# Revit family: Seating_Inc-Hip_Chairs-Cobra-1
name_source: partatom
category: Furniture
revit_build: Autodesk Revit 2014 (Build: 20130308_1515(x64)
units: mm (PartAtom-declared; Revit-internal decimal feet)

## types (4) — shared parameters
Arm Left = Yes
Arm Plastic Finish = STI - Plastic Black
Arm Right = Yes
Assembly Code = E2020200
Back Finish = STI - Upholstery Latex
Depth = 25 1/2"
Glide Finish = STI - Plastic Black
Height = 25"
Keynote = 12500
Low Emitting Finish = Yes
Low Emitting Material = Yes
Manufacturer = Seating Inc
Salvage or Reuse = Yes
Seat Finish = STI - Upholstery Latex
Type Comments = Cobra Tandem Seating
URL = www.seatinginc.com
zero-valued in all types: Percentage of Recycled Content

## per-type parameters (varying)
| type | Arm | Arm Metal Finish | Description | Leg Finish | Support Finish | Width |
| CS444-21B | 23" | STI - Power Coat, Black | Black w/Arms | STI - Power Coat, Black | STI - Power Coat, Black | 23" |
| CS444-21S | 23" | STI - Power Coat, Silver | Silver w/Arms | STI - Power Coat, Silver | STI - Power Coat, Silver | 23" |
| CS444-24B | 26" | STI - Power Coat, Black | Black w/Arms | STI - Power Coat, Black | STI - Power Coat, Black | 26" |
| CS444-24S | 26" | STI - Power Coat, Silver | Silver w/Arms | STI - Power Coat, Silver | STI - Power Coat, Silver | 26" |

note: column(s) folded — value = type name in every type: Model

## geometry (parser evidence)
native form markers: Sweep x3
no freeform markers — native parametric forms only
